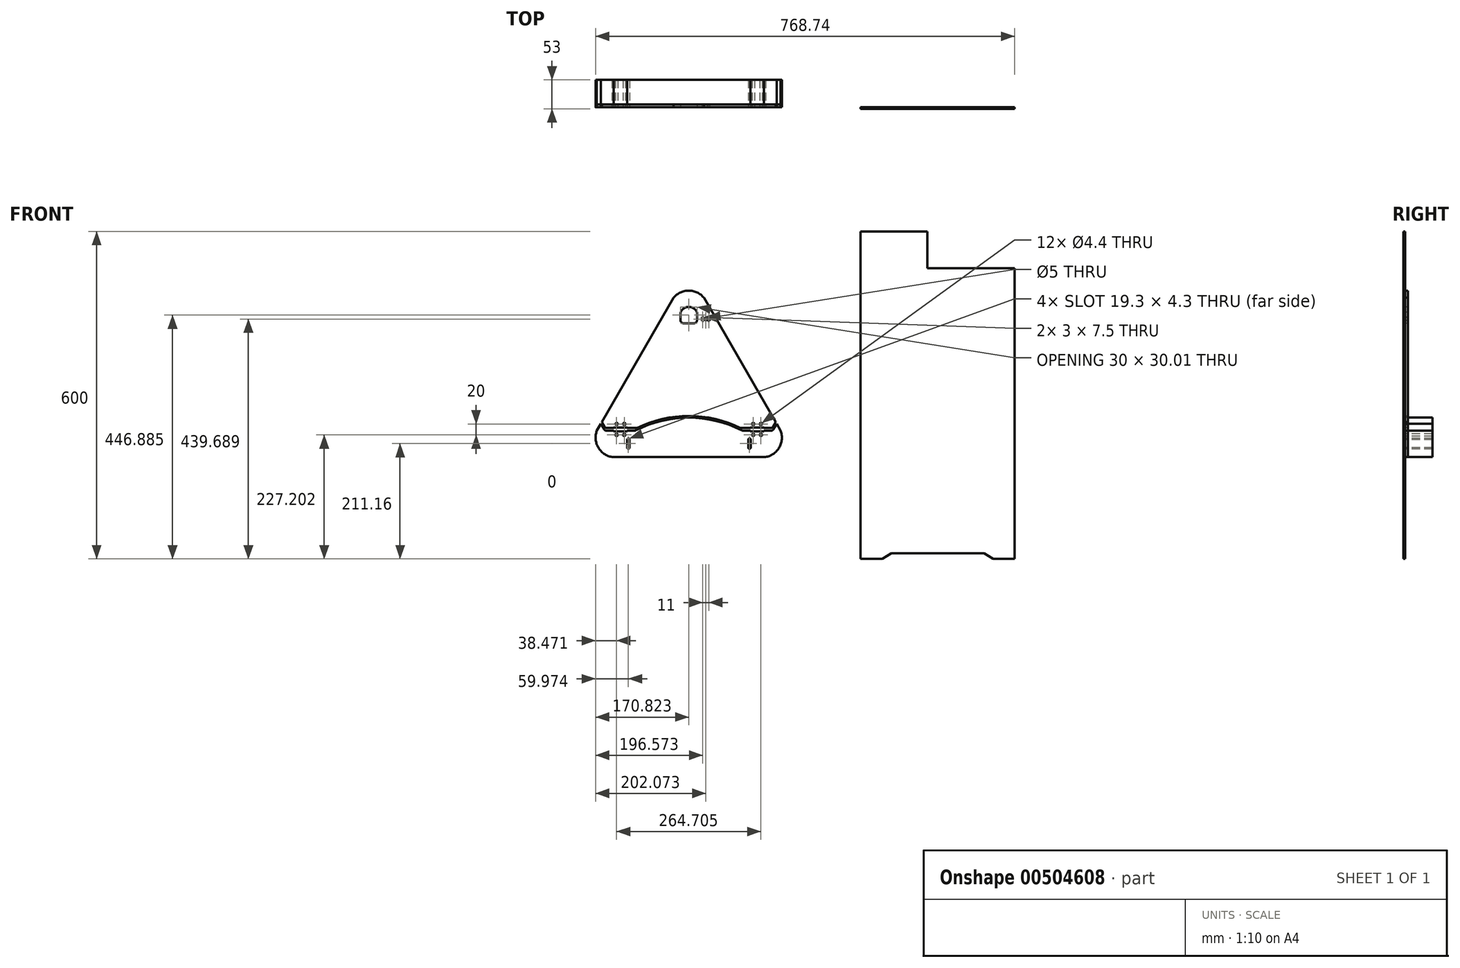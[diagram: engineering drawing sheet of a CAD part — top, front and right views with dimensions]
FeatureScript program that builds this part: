
annotation { "Feature Type Name" : "Feature", "Feature Type Description" : "" }
export const myFeature = defineFeature(function(context is Context, id is Id, definition is map)
    precondition{}
    {
        {
            var Q0;
            Q0=qCreatedBy(makeId("Front.planeOp"),FACE);
            var sketch = newSketch(context, id + "F0", { "sketchPlane" : qUnion([Q0])});
            skLineSegment(sketch, "E0.bottom", {"start": v(-18.5, 300) * mm, "end": v(-141.2, 300) * mm});
            skLineSegment(sketch, "E0.top", {"start": v(141.5, -300) * mm, "end": v(101.5, -300) * mm});
            skLineSegment(sketch, "E0.left", {"start": v(141.5, 233) * mm, "end": v(141.5, -300) * mm});
            skLineSegment(sketch, "E0.right", {"start": v(-141.2, 300) * mm, "end": v(-141.2, -300) * mm});
            skLineSegment(sketch, "E1.top", {"start": v(141.5, 233) * mm, "end": v(-18.5, 233) * mm});
            skLineSegment(sketch, "E1.right", {"start": v(-18.5, 300) * mm, "end": v(-18.5, 233) * mm});
            skLineSegment(sketch, "E2.bottom", {"start": v(186.44, 300) * mm, "end": v(469.14, 300) * mm});
            skLineSegment(sketch, "E2.top", {"start": v(186.44, -300) * mm, "end": v(469.14, -300) * mm});
            skLineSegment(sketch, "E2.left", {"start": v(186.44, 300) * mm, "end": v(186.44, -300) * mm});
            skLineSegment(sketch, "E2.right", {"start": v(469.14, 300) * mm, "end": v(469.14, -300) * mm});
            skLineSegment(sketch, "E3.bottom", {"start": v(-149.47, -443.3) * mm, "end": v(-66.47, -443.3) * mm});
            skLineSegment(sketch, "E3.top", {"start": v(-149.47, -548.3) * mm, "end": v(-71.47, -548.3) * mm});
            skLineSegment(sketch, "E3.left", {"start": v(-149.47, -443.3) * mm, "end": v(-149.47, -548.3) * mm});
            skLineSegment(sketch, "E3.right", {"start": v(-66.47, -443.3) * mm, "end": v(-66.47, -546.3) * mm});
            skLineSegment(sketch, "E4.top", {"start": v(-66.47, -546.3) * mm, "end": v(-71.47, -546.3) * mm});
            skLineSegment(sketch, "E4.right", {"start": v(-71.47, -548.3) * mm, "end": v(-71.47, -546.3) * mm});
            skLineSegment(sketch, "E5.bottom", {"start": v(-34.24, -443.3) * mm, "end": v(248.46, -443.3) * mm});
            skLineSegment(sketch, "E5.top", {"start": v(-34.24, -548.3) * mm, "end": v(248.46, -548.3) * mm});
            skLineSegment(sketch, "E5.left", {"start": v(-34.24, -443.3) * mm, "end": v(-34.24, -548.3) * mm});
            skLineSegment(sketch, "E5.right", {"start": v(248.46, -443.3) * mm, "end": v(248.46, -548.3) * mm});
            skLineSegment(sketch, "E6.bottom", {"start": v(25.76, -515.8) * mm, "end": v(-14.24, -515.8) * mm, "construction": true});
            skLineSegment(sketch, "E6.top", {"start": v(25.76, -475.8) * mm, "end": v(-14.24, -475.8) * mm, "construction": true});
            skLineSegment(sketch, "E6.left", {"start": v(25.76, -515.8) * mm, "end": v(25.76, -475.8) * mm, "construction": true});
            skLineSegment(sketch, "E6.right", {"start": v(-14.24, -515.8) * mm, "end": v(-14.24, -475.8) * mm, "construction": true});
            skPoint(sketch, "E6.middle", {"position": v(5.76, -495.8) * mm});
            skCircle(sketch, "E7", {"center": v(-10.24, -511.8) * mm, "radius": 1.8 * mm});
            skCircle(sketch, "E8.0.1.0", {"center": v(-10.24, -479.8) * mm, "radius": 1.8 * mm});
            skCircle(sketch, "E8.1.0.0", {"center": v(21.76, -511.8) * mm, "radius": 1.8 * mm});
            skCircle(sketch, "E8.1.1.0", {"center": v(21.76, -479.8) * mm, "radius": 1.8 * mm});
            skLineSegment(sketch, "E8.direction1", {"start": v(-10.24, -511.8) * mm, "end": v(21.76, -511.8) * mm, "construction": true});
            skLineSegment(sketch, "E8.direction2", {"start": v(-10.24, -511.8) * mm, "end": v(-10.24, -479.8) * mm, "construction": true});
            skArc(sketch, "E9", {"start": v(-6.6, -509.57) * mm, "mid": v(5.76, -514.3) * mm, "end": v(18.12, -509.57) * mm});
            skLineSegment(sketch, "E10.left", {"start": v(18.12, -482.03) * mm, "end": v(13.51, -486.64) * mm});
            skLineSegment(sketch, "E10.right", {"start": v(19.53, -483.44) * mm, "end": v(14.93, -488.05) * mm});
            skLineSegment(sketch, "E11.left", {"start": v(-8, -483.44) * mm, "end": v(-3.4, -488.05) * mm});
            skLineSegment(sketch, "E11.right", {"start": v(-6.61, -482) * mm, "end": v(-1.99, -486.64) * mm});
            skCircle(sketch, "E12", {"center": v(5.76, -495.8) * mm, "radius": 11 * mm, "construction": true});
            skArc(sketch, "E13.0", {"start": v(-3.4, -488.05) * mm, "mid": v(-6.24, -495.8) * mm, "end": v(-3.4, -503.55) * mm});
            skArc(sketch, "E14.0", {"start": v(-1.98, -489.47) * mm, "mid": v(-4.24, -495.8) * mm, "end": v(-1.98, -502.13) * mm});
            skLineSegment(sketch, "E15.right", {"start": v(141.46, -473.3) * mm, "end": v(141.46, -518.3) * mm, "construction": true});
            skArc(sketch, "E16.0.startCap", {"start": v(134.96, -473.3) * mm, "mid": v(141.46, -466.8) * mm, "end": v(147.96, -473.3) * mm});
            skArc(sketch, "E16.0.endCap", {"start": v(147.96, -518.3) * mm, "mid": v(141.46, -524.8) * mm, "end": v(134.96, -518.3) * mm});
            skLineSegment(sketch, "E16.0.left", {"start": v(147.96, -473.3) * mm, "end": v(147.96, -518.3) * mm});
            skLineSegment(sketch, "E16.0.right", {"start": v(134.96, -473.3) * mm, "end": v(134.96, -518.3) * mm});
            skLineSegment(sketch, "E17.bottom", {"start": v(279.2, -443.3) * mm, "end": v(561.9, -443.3) * mm});
            skLineSegment(sketch, "E17.top", {"start": v(279.2, -548.3) * mm, "end": v(404.2, -548.3) * mm});
            skLineSegment(sketch, "E17.left", {"start": v(279.2, -443.3) * mm, "end": v(279.2, -548.3) * mm});
            skLineSegment(sketch, "E17.right", {"start": v(561.9, -443.3) * mm, "end": v(561.9, -537.3) * mm});
            skLineSegment(sketch, "E18.top", {"start": v(561.9, -537.3) * mm, "end": v(552.9, -537.3) * mm});
            skLineSegment(sketch, "E18.right", {"start": v(404.2, -548.3) * mm, "end": v(404.2, -537.3) * mm});
            skEllipse(sketch, "E19", {"center": v(198.94, 200) * mm, "majorRadius": 3.5 * mm, "minorRadius": 2.5 * mm, "majorAxis": v(1, 0)});
            skEllipse(sketch, "E20.1.0.0", {"center": v(216.44, 200) * mm, "majorRadius": 3.5 * mm, "minorRadius": 2.5 * mm, "majorAxis": v(1, 0)});
            skLineSegment(sketch, "E20.direction1", {"start": v(198.94, 200) * mm, "end": v(216.44, 200) * mm, "construction": true});
            skCircle(sketch, "E21", {"center": v(198.94, 200) * mm, "radius": 2.5 * mm, "construction": true});
            skCircle(sketch, "E22", {"center": v(216.44, 200) * mm, "radius": 2.5 * mm, "construction": true});
            skEllipse(sketch, "E23", {"center": v(439.14, 200) * mm, "majorRadius": 3.5 * mm, "minorRadius": 2.5 * mm, "majorAxis": v(1, 0)});
            skEllipse(sketch, "E24.1.0.0", {"center": v(456.64, 200) * mm, "majorRadius": 3.5 * mm, "minorRadius": 2.5 * mm, "majorAxis": v(1, 0)});
            skLineSegment(sketch, "E24.direction1", {"start": v(439.14, 200) * mm, "end": v(456.64, 200) * mm, "construction": true});
            skCircle(sketch, "E25", {"center": v(439.14, 200) * mm, "radius": 2.5 * mm, "construction": true});
            skCircle(sketch, "E26", {"center": v(456.64, 200) * mm, "radius": 2.5 * mm, "construction": true});
            skEllipse(sketch, "E27", {"center": v(198.94, -200) * mm, "majorRadius": 3.5 * mm, "minorRadius": 2.5 * mm, "majorAxis": v(1, 0)});
            skEllipse(sketch, "E28.1.0.0", {"center": v(216.44, -200) * mm, "majorRadius": 3.5 * mm, "minorRadius": 2.5 * mm, "majorAxis": v(1, 0)});
            skLineSegment(sketch, "E28.direction1", {"start": v(198.94, -200) * mm, "end": v(216.44, -200) * mm, "construction": true});
            skCircle(sketch, "E29", {"center": v(198.94, -200) * mm, "radius": 2.5 * mm, "construction": true});
            skCircle(sketch, "E30", {"center": v(216.44, -200) * mm, "radius": 2.5 * mm, "construction": true});
            skEllipse(sketch, "E31", {"center": v(439.14, -200) * mm, "majorRadius": 3.5 * mm, "minorRadius": 2.5 * mm, "majorAxis": v(1, 0)});
            skEllipse(sketch, "E32.1.0.0", {"center": v(456.64, -200) * mm, "majorRadius": 3.5 * mm, "minorRadius": 2.5 * mm, "majorAxis": v(1, 0)});
            skLineSegment(sketch, "E32.direction1", {"start": v(439.14, -200) * mm, "end": v(456.64, -200) * mm, "construction": true});
            skCircle(sketch, "E33", {"center": v(439.14, -200) * mm, "radius": 2.5 * mm, "construction": true});
            skCircle(sketch, "E34", {"center": v(456.64, -200) * mm, "radius": 2.5 * mm, "construction": true});
            skLineSegment(sketch, "E35.1.0.0", {"start": v(771.14, 300) * mm, "end": v(771.14, -300) * mm});
            skLineSegment(sketch, "E35.1.0.1", {"start": v(488.44, -300) * mm, "end": v(771.14, -300) * mm});
            skLineSegment(sketch, "E35.1.0.2", {"start": v(488.44, 300) * mm, "end": v(771.14, 300) * mm});
            skLineSegment(sketch, "E35.1.0.3", {"start": v(488.44, 300) * mm, "end": v(488.44, -300) * mm});
            skCircle(sketch, "E35.1.0.4", {"center": v(518.44, -200) * mm, "radius": 2.5 * mm, "construction": true});
            skCircle(sketch, "E35.1.0.5", {"center": v(758.64, -200) * mm, "radius": 2.5 * mm, "construction": true});
            skLineSegment(sketch, "E35.1.0.6", {"start": v(500.94, -200) * mm, "end": v(518.44, -200) * mm, "construction": true});
            skEllipse(sketch, "E35.1.0.7", {"center": v(518.44, 200) * mm, "majorRadius": 3.5 * mm, "minorRadius": 2.5 * mm, "majorAxis": v(1, 0)});
            skEllipse(sketch, "E35.1.0.8", {"center": v(500.94, -200) * mm, "majorRadius": 3.5 * mm, "minorRadius": 2.5 * mm, "majorAxis": v(1, 0)});
            skCircle(sketch, "E35.1.0.9", {"center": v(500.94, 200) * mm, "radius": 2.5 * mm, "construction": true});
            skEllipse(sketch, "E35.1.0.10", {"center": v(518.44, -200) * mm, "majorRadius": 3.5 * mm, "minorRadius": 2.5 * mm, "majorAxis": v(1, 0)});
            skCircle(sketch, "E35.1.0.11", {"center": v(758.64, 200) * mm, "radius": 2.5 * mm, "construction": true});
            skCircle(sketch, "E35.1.0.12", {"center": v(500.94, -200) * mm, "radius": 2.5 * mm, "construction": true});
            skCircle(sketch, "E35.1.0.13", {"center": v(518.44, 200) * mm, "radius": 2.5 * mm, "construction": true});
            skEllipse(sketch, "E35.1.0.14", {"center": v(500.94, 200) * mm, "majorRadius": 3.5 * mm, "minorRadius": 2.5 * mm, "majorAxis": v(1, 0)});
            skLineSegment(sketch, "E35.1.0.15", {"start": v(500.94, 200) * mm, "end": v(518.44, 200) * mm, "construction": true});
            skCircle(sketch, "E35.1.0.16", {"center": v(741.14, 200) * mm, "radius": 2.5 * mm, "construction": true});
            skCircle(sketch, "E35.1.0.17", {"center": v(741.14, -200) * mm, "radius": 2.5 * mm, "construction": true});
            skEllipse(sketch, "E35.1.0.18", {"center": v(758.64, 200) * mm, "majorRadius": 3.5 * mm, "minorRadius": 2.5 * mm, "majorAxis": v(1, 0)});
            skLineSegment(sketch, "E35.1.0.19", {"start": v(741.14, -200) * mm, "end": v(758.64, -200) * mm, "construction": true});
            skLineSegment(sketch, "E35.1.0.20", {"start": v(741.14, 200) * mm, "end": v(758.64, 200) * mm, "construction": true});
            skEllipse(sketch, "E35.1.0.21", {"center": v(758.64, -200) * mm, "majorRadius": 3.5 * mm, "minorRadius": 2.5 * mm, "majorAxis": v(1, 0)});
            skEllipse(sketch, "E35.1.0.22", {"center": v(741.14, -200) * mm, "majorRadius": 3.5 * mm, "minorRadius": 2.5 * mm, "majorAxis": v(1, 0)});
            skEllipse(sketch, "E35.1.0.23", {"center": v(741.14, 200) * mm, "majorRadius": 3.5 * mm, "minorRadius": 2.5 * mm, "majorAxis": v(1, 0)});
            skLineSegment(sketch, "E35.direction1", {"start": v(186.44, -300) * mm, "end": v(488.44, -300) * mm, "construction": true});
            skEllipse(sketch, "E36", {"center": v(531.9, -458.3) * mm, "majorRadius": 3.5 * mm, "minorRadius": 2.5 * mm, "majorAxis": v(1, 0)});
            skEllipse(sketch, "E37.1.0.0", {"center": v(549.4, -458.3) * mm, "majorRadius": 3.5 * mm, "minorRadius": 2.5 * mm, "majorAxis": v(1, 0), "construction": true});
            skLineSegment(sketch, "E37.direction1", {"start": v(531.9, -458.3) * mm, "end": v(549.4, -458.3) * mm, "construction": true});
            skCircle(sketch, "E38", {"center": v(531.9, -458.3) * mm, "radius": 2.5 * mm, "construction": true});
            skCircle(sketch, "E39", {"center": v(549.4, -458.3) * mm, "radius": 2.5 * mm, "construction": true});
            skCircle(sketch, "E40", {"center": v(549.4, -458.3) * mm, "radius": 1.75 * mm});
            skCircle(sketch, "E41", {"center": v(458.4, -458.3) * mm, "radius": 1.75 * mm});
            skLineSegment(sketch, "E42", {"start": v(458.4, -458.3) * mm, "end": v(576.67, -458.3) * mm, "construction": true});
            skEllipse(sketch, "E43", {"center": v(291.7, -458.3) * mm, "majorRadius": 3.5 * mm, "minorRadius": 2.5 * mm, "majorAxis": v(1, 0)});
            skEllipse(sketch, "E44.1.0.0", {"center": v(309.2, -458.3) * mm, "majorRadius": 3.5 * mm, "minorRadius": 2.5 * mm, "majorAxis": v(1, 0)});
            skLineSegment(sketch, "E44.direction1", {"start": v(291.7, -458.3) * mm, "end": v(309.2, -458.3) * mm, "construction": true});
            skCircle(sketch, "E45", {"center": v(291.7, -458.3) * mm, "radius": 2.5 * mm, "construction": true});
            skCircle(sketch, "E46", {"center": v(309.2, -458.3) * mm, "radius": 2.5 * mm, "construction": true});
            skEllipse(sketch, "E47", {"center": v(218.46, -458.3) * mm, "majorRadius": 3.5 * mm, "minorRadius": 2.5 * mm, "majorAxis": v(1, 0)});
            skEllipse(sketch, "E48.1.0.0", {"center": v(235.96, -458.3) * mm, "majorRadius": 3.5 * mm, "minorRadius": 2.5 * mm, "majorAxis": v(1, 0)});
            skLineSegment(sketch, "E48.direction1", {"start": v(218.46, -458.3) * mm, "end": v(235.96, -458.3) * mm, "construction": true});
            skCircle(sketch, "E49", {"center": v(218.46, -458.3) * mm, "radius": 2.5 * mm, "construction": true});
            skCircle(sketch, "E50", {"center": v(235.96, -458.3) * mm, "radius": 2.5 * mm, "construction": true});
            skEllipse(sketch, "E51", {"center": v(218.46, -534.3) * mm, "majorRadius": 3.5 * mm, "minorRadius": 2.5 * mm, "majorAxis": v(1, 0)});
            skEllipse(sketch, "E52.1.0.0", {"center": v(235.96, -534.3) * mm, "majorRadius": 3.5 * mm, "minorRadius": 2.5 * mm, "majorAxis": v(1, 0)});
            skLineSegment(sketch, "E52.direction1", {"start": v(218.46, -534.3) * mm, "end": v(235.96, -534.3) * mm, "construction": true});
            skCircle(sketch, "E53", {"center": v(218.46, -534.3) * mm, "radius": 2.5 * mm, "construction": true});
            skCircle(sketch, "E54", {"center": v(235.96, -534.3) * mm, "radius": 2.5 * mm, "construction": true});
            skEllipse(sketch, "E55", {"center": v(291.7, -534.3) * mm, "majorRadius": 3.5 * mm, "minorRadius": 2.5 * mm, "majorAxis": v(1, 0)});
            skEllipse(sketch, "E56.1.0.0", {"center": v(309.2, -534.3) * mm, "majorRadius": 3.5 * mm, "minorRadius": 2.5 * mm, "majorAxis": v(1, 0)});
            skLineSegment(sketch, "E56.direction1", {"start": v(291.7, -534.3) * mm, "end": v(309.2, -534.3) * mm, "construction": true});
            skCircle(sketch, "E57", {"center": v(291.7, -534.3) * mm, "radius": 2.5 * mm, "construction": true});
            skCircle(sketch, "E58", {"center": v(309.2, -534.3) * mm, "radius": 2.5 * mm, "construction": true});
            skEllipticalArc(sketch, "E59", {});
            skEllipticalArc(sketch, "E60.1.0.0", {});
            skLineSegment(sketch, "E60.direction1", {"start": v(531.9, -534.3) * mm, "end": v(549.4, -534.3) * mm, "construction": true});
            skCircle(sketch, "E61", {"center": v(531.9, -534.3) * mm, "radius": 2.5 * mm, "construction": true});
            skCircle(sketch, "E62", {"center": v(549.4, -534.3) * mm, "radius": 2.5 * mm, "construction": true});
            skEllipse(sketch, "E63", {"center": v(-21.74, -458.3) * mm, "majorRadius": 3.5 * mm, "minorRadius": 2.5 * mm, "majorAxis": v(1, 0)});
            skEllipse(sketch, "E64.1.0.0", {"center": v(-4.24, -458.3) * mm, "majorRadius": 3.5 * mm, "minorRadius": 2.5 * mm, "majorAxis": v(1, 0)});
            skLineSegment(sketch, "E64.direction1", {"start": v(-21.74, -458.3) * mm, "end": v(-4.24, -458.3) * mm, "construction": true});
            skCircle(sketch, "E65", {"center": v(-21.74, -458.3) * mm, "radius": 2.5 * mm, "construction": true});
            skCircle(sketch, "E66", {"center": v(-4.24, -458.3) * mm, "radius": 2.5 * mm, "construction": true});
            skEllipse(sketch, "E67", {"center": v(-21.74, -534.3) * mm, "majorRadius": 3.5 * mm, "minorRadius": 2.5 * mm, "majorAxis": v(1, 0)});
            skEllipse(sketch, "E68.1.0.0", {"center": v(-4.24, -534.3) * mm, "majorRadius": 3.5 * mm, "minorRadius": 2.5 * mm, "majorAxis": v(1, 0)});
            skLineSegment(sketch, "E68.direction1", {"start": v(-21.74, -534.3) * mm, "end": v(-4.24, -534.3) * mm, "construction": true});
            skCircle(sketch, "E69", {"center": v(-21.74, -534.3) * mm, "radius": 2.5 * mm, "construction": true});
            skCircle(sketch, "E70", {"center": v(-4.24, -534.3) * mm, "radius": 2.5 * mm, "construction": true});
            skEllipse(sketch, "E71", {"center": v(-136.97, -458.3) * mm, "majorRadius": 3.5 * mm, "minorRadius": 2.5 * mm, "majorAxis": v(1, 0)});
            skEllipse(sketch, "E72.1.0.0", {"center": v(-119.47, -458.3) * mm, "majorRadius": 3.5 * mm, "minorRadius": 2.5 * mm, "majorAxis": v(1, 0)});
            skLineSegment(sketch, "E72.direction1", {"start": v(-136.97, -458.3) * mm, "end": v(-119.47, -458.3) * mm, "construction": true});
            skCircle(sketch, "E73", {"center": v(-136.97, -458.3) * mm, "radius": 2.5 * mm, "construction": true});
            skCircle(sketch, "E74", {"center": v(-119.47, -458.3) * mm, "radius": 2.5 * mm, "construction": true});
            skEllipse(sketch, "E75", {"center": v(-136.97, -534.3) * mm, "majorRadius": 3.5 * mm, "minorRadius": 2.5 * mm, "majorAxis": v(1, 0)});
            skEllipse(sketch, "E76.1.0.0", {"center": v(-119.47, -534.3) * mm, "majorRadius": 3.5 * mm, "minorRadius": 2.5 * mm, "majorAxis": v(1, 0)});
            skLineSegment(sketch, "E76.direction1", {"start": v(-136.97, -534.3) * mm, "end": v(-119.47, -534.3) * mm, "construction": true});
            skCircle(sketch, "E77", {"center": v(-136.97, -534.3) * mm, "radius": 2.5 * mm, "construction": true});
            skCircle(sketch, "E78", {"center": v(-119.47, -534.3) * mm, "radius": 2.5 * mm, "construction": true});
            skLineSegment(sketch, "E79", {"start": v(528.4, -534.3) * mm, "end": v(528.4, -537.3) * mm});
            skLineSegment(sketch, "E80", {"start": v(535.4, -534.3) * mm, "end": v(535.4, -537.3) * mm});
            skLineSegment(sketch, "E81", {"start": v(545.9, -534.3) * mm, "end": v(545.9, -537.3) * mm});
            skLineSegment(sketch, "E82", {"start": v(552.9, -534.3) * mm, "end": v(552.9, -537.3) * mm});
            skLineSegment(sketch, "E83.trimOffspring", {"start": v(528.4, -537.3) * mm, "end": v(404.2, -537.3) * mm});
            skLineSegment(sketch, "E84.trimOffspring", {"start": v(545.9, -537.3) * mm, "end": v(535.4, -537.3) * mm});
            skLineSegment(sketch, "E85", {"start": v(-85, -290) * mm, "end": v(85, -290) * mm});
            skPoint(sketch, "E86", {"position": v(0, -290) * mm});
            skPoint(sketch, "E87", {"position": v(-101.2, -300) * mm});
            skLineSegment(sketch, "E88", {"start": v(-101.2, -300) * mm, "end": v(-85, -290) * mm});
            skLineSegment(sketch, "E89.trimOffspring", {"start": v(-101.2, -300) * mm, "end": v(-141.2, -300) * mm});
            skPoint(sketch, "E90", {"position": v(101.5, -300) * mm});
            skLineSegment(sketch, "E91", {"start": v(85, -290) * mm, "end": v(101.5, -300) * mm});
            skLineSegment(sketch, "E92.trimOffspring", {"start": v(7.18, -495.8) * mm, "end": v(13.5, -502.13) * mm});
            skLineSegment(sketch, "E93.trimOffspring", {"start": v(5.76, -497.21) * mm, "end": v(12.1, -503.54) * mm});
            skLineSegment(sketch, "E94.trimOffspring", {"start": v(4.35, -495.8) * mm, "end": v(-1.98, -502.13) * mm});
            skLineSegment(sketch, "E95.trimOffspring", {"start": v(5.76, -497.21) * mm, "end": v(-0.57, -503.54) * mm});
            skArc(sketch, "E96.trimOffspring", {"start": v(19.53, -508.15) * mm, "mid": v(24.26, -495.8) * mm, "end": v(19.53, -483.44) * mm});
            skArc(sketch, "E97.trimOffspring", {"start": v(18.12, -482.03) * mm, "mid": v(5.76, -477.3) * mm, "end": v(-6.6, -482.03) * mm});
            skArc(sketch, "E98.trimOffspring", {"start": v(-8, -483.44) * mm, "mid": v(-12.74, -495.8) * mm, "end": v(-8, -508.15) * mm});
            skCircle(sketch, "E99.0.1.0", {"center": v(458.4, -534.3) * mm, "radius": 1.75 * mm});
            skLineSegment(sketch, "E99.direction1", {"start": v(458.4, -458.3) * mm, "end": v(483.4, -458.3) * mm, "construction": true});
            skLineSegment(sketch, "E99.direction2", {"start": v(458.4, -458.3) * mm, "end": v(458.4, -534.3) * mm, "construction": true});
            skLineSegment(sketch, "E100.trimOffspring", {"start": v(-3.4, -503.55) * mm, "end": v(-8, -508.15) * mm});
            skLineSegment(sketch, "E101.trimOffspring", {"start": v(-1.99, -504.96) * mm, "end": v(-6.6, -509.57) * mm});
            skLineSegment(sketch, "E102.trimOffspring", {"start": v(14.93, -503.55) * mm, "end": v(19.55, -508.17) * mm});
            skLineSegment(sketch, "E103.trimOffspring", {"start": v(13.51, -504.96) * mm, "end": v(18.14, -509.59) * mm});
            skLineSegment(sketch, "E104.trimOffspring", {"start": v(-0.57, -488.06) * mm, "end": v(5.76, -494.38) * mm});
            skLineSegment(sketch, "E105.trimOffspring", {"start": v(-1.98, -489.47) * mm, "end": v(4.35, -495.8) * mm});
            skLineSegment(sketch, "E106.trimOffspring", {"start": v(12.1, -488.06) * mm, "end": v(5.76, -494.38) * mm});
            skLineSegment(sketch, "E107.trimOffspring", {"start": v(13.5, -489.47) * mm, "end": v(7.18, -495.8) * mm});
            skArc(sketch, "E108.trimOffspring", {"start": v(12.1, -488.06) * mm, "mid": v(5.76, -485.8) * mm, "end": v(-0.57, -488.06) * mm});
            skArc(sketch, "E109.trimOffspring", {"start": v(13.51, -486.64) * mm, "mid": v(5.76, -483.8) * mm, "end": v(-1.99, -486.64) * mm});
            skArc(sketch, "E110.trimOffspring", {"start": v(13.5, -502.13) * mm, "mid": v(15.76, -495.8) * mm, "end": v(13.5, -489.47) * mm});
            skArc(sketch, "E111.trimOffspring", {"start": v(14.93, -503.55) * mm, "mid": v(17.76, -495.8) * mm, "end": v(14.93, -488.05) * mm});
            skArc(sketch, "E112.trimOffspring", {"start": v(-1.99, -504.96) * mm, "mid": v(5.76, -507.8) * mm, "end": v(13.51, -504.96) * mm});
            skArc(sketch, "E113.trimOffspring", {"start": v(-0.57, -503.54) * mm, "mid": v(5.76, -505.8) * mm, "end": v(12.1, -503.54) * mm});
            const initialGuessF0  = {"E59": [0.5318984677314759, -0.5342984781265259, 1, 0, 0.0035, 0.0025, 0, 3.141592653589793], "E60.1.0.0": [0.5493984677314758, -0.5342984781265259, 1, 0, 0.0035, 0.0025, 0, 3.141592653589793]};
            skSetInitialGuess(sketch, initialGuessF0);
            skSolve(sketch);
        }
        {
            var Q0;
            Q0=makeQuery(id+"F0.imprint","IMPRINT",FACE,{"disambiguationData":[TD([[makeQuery(id+"F0.imprint","IMPRINT",EDGE,{"derivedFrom":sQuery(id+"F0.wireOp",EDGE,"E0.bottom")}),1.0]])]});
            extrude(context, id + "F1", {"entities" : qUnion([Q0]), "depth" : 3 * mm});
        }
        {
            var Q0;
            Q0=qCreatedBy(makeId("Front.planeOp"),FACE);
            var sketch = newSketch(context, id + "F2", { "sketchPlane" : qUnion([Q0])});
            skLineSegment(sketch, "E114", {"start": v(-567.99, 54.45) * mm, "end": v(-344.84, 54.45) * mm, "construction": true});
            skLineSegment(sketch, "E115", {"start": v(-456.42, 178.66) * mm, "end": v(-456.42, 161.88) * mm, "construction": true});
            skArc(sketch, "E116", {"start": v(-428.67, 178.66) * mm, "mid": v(-456.42, 191.66) * mm, "end": v(-484.17, 178.66) * mm});
            skLineSegment(sketch, "E117", {"start": v(-597.77, -113.34) * mm, "end": v(-315.07, -113.34) * mm, "construction": true});
            skArc(sketch, "E118.1.0", {"start": v(-625.02, -65.3) * mm, "mid": v(-622.4, -95.83) * mm, "end": v(-597.27, -113.36) * mm});
            skArc(sketch, "E118.2.0", {"start": v(-315.57, -113.36) * mm, "mid": v(-290.43, -95.83) * mm, "end": v(-287.82, -65.3) * mm});
            skPoint(sketch, "E118.center", {"position": v(-456.42, 0) * mm});
            skLineSegment(sketch, "E119", {"start": v(-290.75, -60.21) * mm, "end": v(-295.28, -52.38) * mm});
            skLineSegment(sketch, "E120", {"start": v(-315.57, -113.36) * mm, "end": v(-597.27, -113.36) * mm});
            skLineSegment(sketch, "E121", {"start": v(-622.18, -60.38) * mm, "end": v(-617.56, -52.38) * mm});
            skLineSegment(sketch, "E122", {"start": v(-607.2, -65.3) * mm, "end": v(-594.22, -65.3) * mm});
            skLineSegment(sketch, "E123.bottom", {"start": v(-456, 161.88) * mm, "end": v(-456.84, 161.88) * mm});
            skLineSegment(sketch, "E123.top", {"start": v(-446.42, 131.88) * mm, "end": v(-466.42, 131.88) * mm});
            skLineSegment(sketch, "E123.left", {"start": v(-441.42, 151.88) * mm, "end": v(-441.42, 136.88) * mm});
            skLineSegment(sketch, "E123.right", {"start": v(-471.42, 151.88) * mm, "end": v(-471.42, 136.88) * mm});
            skPoint(sketch, "E123.middle", {"position": v(-456.42, 146.88) * mm});
            skArc(sketch, "E124", {"start": v(-441.42, 151.88) * mm, "mid": v(-456.42, 161.89) * mm, "end": v(-471.42, 151.88) * mm});
            skPoint(sketch, "E125.orphan", {"position": v(-471.42, 161.88) * mm});
            skPoint(sketch, "E126.orphan", {"position": v(-441.42, 161.88) * mm});
            skLineSegment(sketch, "E127.trimOffspring", {"start": v(-456.42, 54.45) * mm, "end": v(-456.42, -113.34) * mm, "construction": true});
            skArc(sketch, "E128", {"start": v(-358.88, -64.75) * mm, "mid": v(-456.42, -41.2) * mm, "end": v(-553.95, -64.75) * mm});
            skArc(sketch, "E129.0", {"start": v(-362.08, -59.8) * mm, "mid": v(-456.42, -38.2) * mm, "end": v(-550.75, -59.8) * mm});
            skLineSegment(sketch, "E130.trimOffspring", {"start": v(-359.9, -60.3) * mm, "end": v(-343.61, -60.3) * mm});
            skLineSegment(sketch, "E131", {"start": v(-625.02, -65.3) * mm, "end": v(-597.27, -113.36) * mm, "construction": true});
            skLineSegment(sketch, "E132", {"start": v(-315.02, -113.26) * mm, "end": v(-315.07, -113.34) * mm});
            skLineSegment(sketch, "E133", {"start": v(-617.56, -52.38) * mm, "end": v(-613.06, -60.17) * mm});
            skLineSegment(sketch, "E134.0", {"start": v(-615.82, -49.38) * mm, "end": v(-610.96, -57.8) * mm});
            skLineSegment(sketch, "E135", {"start": v(-625.02, -65.3) * mm, "end": v(-622.18, -60.38) * mm});
            skLineSegment(sketch, "E136", {"start": v(-578.9, -113.34) * mm, "end": v(-578.88, -113.36) * mm});
            skLineSegment(sketch, "E137", {"start": v(-610.1, -65.3) * mm, "end": v(-582.34, -113.36) * mm, "construction": true});
            skLineSegment(sketch, "E138", {"start": v(-613.06, -60.17) * mm, "end": v(-611.54, -62.8) * mm});
            skLineSegment(sketch, "E139.trimOffspring", {"start": v(-615.82, -49.38) * mm, "end": v(-484.17, 178.66) * mm});
            skLineSegment(sketch, "E140.trimOffspring", {"start": v(-606.63, -60.3) * mm, "end": v(-594.22, -60.3) * mm});
            skLineSegment(sketch, "E141.trimOffspring", {"start": v(-356.6, -65.3) * mm, "end": v(-343.61, -65.3) * mm});
            skLineSegment(sketch, "E142.MirrorCS", {"start": v(-602.63, -52.38) * mm, "end": v(-574.88, -100.44) * mm, "construction": true});
            skLineSegment(sketch, "E143.MirrorCS", {"start": v(-302.74, -65.3) * mm, "end": v(-330.49, -113.36) * mm, "construction": true});
            skLineSegment(sketch, "E144.MirrorCS", {"start": v(-297.01, -49.38) * mm, "end": v(-301.87, -57.8) * mm});
            skLineSegment(sketch, "E145", {"start": v(-301.3, -62.8) * mm, "end": v(-295.28, -52.38) * mm});
            skLineSegment(sketch, "E146", {"start": v(-290.75, -60.21) * mm, "end": v(-287.82, -65.3) * mm});
            skLineSegment(sketch, "E147.trimOffspring", {"start": v(-297.01, -49.38) * mm, "end": v(-428.67, 178.66) * mm});
            skPoint(sketch, "E148.visualSharp", {"position": v(-610.1, -65.3) * mm});
            skArc(sketch, "E148.filletArc", {"start": v(-611.54, -62.8) * mm, "mid": v(-609.7, -64.63) * mm, "end": v(-607.2, -65.3) * mm});
            skPoint(sketch, "E149.visualSharp", {"position": v(-609.52, -60.3) * mm});
            skArc(sketch, "E149.filletArc", {"start": v(-610.96, -57.8) * mm, "mid": v(-609.13, -59.63) * mm, "end": v(-606.63, -60.3) * mm});
            skPoint(sketch, "E150.visualSharp", {"position": v(-551.77, -60.3) * mm});
            skArc(sketch, "E150.filletArc", {"start": v(-552.93, -60.3) * mm, "mid": v(-551.8, -60.17) * mm, "end": v(-550.75, -59.8) * mm});
            skPoint(sketch, "E151.visualSharp", {"position": v(-555.02, -65.3) * mm});
            skArc(sketch, "E151.filletArc", {"start": v(-556.23, -65.3) * mm, "mid": v(-555.06, -65.16) * mm, "end": v(-553.95, -64.75) * mm});
            skPoint(sketch, "E152.visualSharp", {"position": v(-361.06, -60.3) * mm});
            skArc(sketch, "E152.filletArc", {"start": v(-362.08, -59.8) * mm, "mid": v(-361.02, -60.17) * mm, "end": v(-359.9, -60.3) * mm});
            skPoint(sketch, "E153.visualSharp", {"position": v(-357.82, -65.3) * mm});
            skArc(sketch, "E153.filletArc", {"start": v(-358.88, -64.75) * mm, "mid": v(-357.78, -65.16) * mm, "end": v(-356.6, -65.3) * mm});
            skPoint(sketch, "E154.visualSharp", {"position": v(-303.32, -60.3) * mm});
            skArc(sketch, "E154.filletArc", {"start": v(-306.2, -60.3) * mm, "mid": v(-303.7, -59.63) * mm, "end": v(-301.87, -57.8) * mm});
            skPoint(sketch, "E155.visualSharp", {"position": v(-302.74, -65.3) * mm});
            skArc(sketch, "E155.filletArc", {"start": v(-305.63, -65.3) * mm, "mid": v(-303.13, -64.63) * mm, "end": v(-301.3, -62.8) * mm});
            skPoint(sketch, "E156.visualSharp", {"position": v(-471.42, 131.88) * mm});
            skArc(sketch, "E156.filletArc", {"start": v(-471.42, 136.88) * mm, "mid": v(-469.95, 133.35) * mm, "end": v(-466.42, 131.88) * mm});
            skPoint(sketch, "E157.visualSharp", {"position": v(-441.42, 131.88) * mm});
            skArc(sketch, "E157.filletArc", {"start": v(-446.42, 131.88) * mm, "mid": v(-442.88, 133.35) * mm, "end": v(-441.42, 136.88) * mm});
            skPoint(sketch, "E158", {"position": v(-581.72, -65.3) * mm});
            skCircle(sketch, "E159", {"center": v(-588.77, -72.8) * mm, "radius": 2.2 * mm});
            skCircle(sketch, "E160", {"center": v(-574.67, -72.8) * mm, "radius": 2.2 * mm});
            skLineSegment(sketch, "E161", {"start": v(-588.77, -72.8) * mm, "end": v(-574.67, -72.8) * mm, "construction": true});
            skPoint(sketch, "E162", {"position": v(-581.72, -72.8) * mm});
            skCircle(sketch, "E163.0.1.0", {"center": v(-588.77, -52.8) * mm, "radius": 2.2 * mm});
            skCircle(sketch, "E163.0.1.1", {"center": v(-574.67, -52.8) * mm, "radius": 2.2 * mm});
            skLineSegment(sketch, "E163.direction1", {"start": v(-588.77, -72.8) * mm, "end": v(-562.72, -72.8) * mm, "construction": true});
            skLineSegment(sketch, "E163.direction2", {"start": v(-588.77, -72.8) * mm, "end": v(-588.77, -52.8) * mm, "construction": true});
            skPoint(sketch, "E164", {"position": v(-569.22, -65.3) * mm});
            skPoint(sketch, "E165", {"position": v(-594.22, -65.3) * mm});
            skPoint(sketch, "E166", {"position": v(-594.22, -60.3) * mm});
            skPoint(sketch, "E167", {"position": v(-569.22, -60.3) * mm});
            skLineSegment(sketch, "E168", {"start": v(-594.22, -60.3) * mm, "end": v(-594.22, -59.3) * mm});
            skLineSegment(sketch, "E169", {"start": v(-594.22, -59.3) * mm, "end": v(-569.22, -59.3) * mm});
            skLineSegment(sketch, "E170", {"start": v(-569.22, -59.3) * mm, "end": v(-569.22, -60.3) * mm});
            skLineSegment(sketch, "E171", {"start": v(-594.22, -65.3) * mm, "end": v(-594.22, -66.36) * mm});
            skLineSegment(sketch, "E172", {"start": v(-594.22, -66.36) * mm, "end": v(-569.22, -66.36) * mm});
            skLineSegment(sketch, "E173", {"start": v(-569.22, -66.36) * mm, "end": v(-569.22, -65.3) * mm});
            skLineSegment(sketch, "E174.trimOffspring", {"start": v(-569.22, -60.3) * mm, "end": v(-552.93, -60.3) * mm});
            skLineSegment(sketch, "E175.trimOffspring", {"start": v(-569.22, -65.3) * mm, "end": v(-556.23, -65.3) * mm});
            skPoint(sketch, "E176", {"position": v(-331.11, -65.3) * mm});
            skCircle(sketch, "E177.1.0.0", {"center": v(-338.16, -52.8) * mm, "radius": 2.2 * mm});
            skCircle(sketch, "E177.1.0.1", {"center": v(-324.06, -52.8) * mm, "radius": 2.2 * mm});
            skLineSegment(sketch, "E177.1.0.2", {"start": v(-343.61, -59.3) * mm, "end": v(-318.61, -59.3) * mm});
            skLineSegment(sketch, "E177.1.0.3", {"start": v(-343.61, -66.36) * mm, "end": v(-318.61, -66.36) * mm});
            skCircle(sketch, "E177.1.0.4", {"center": v(-338.16, -72.8) * mm, "radius": 2.2 * mm});
            skCircle(sketch, "E177.1.0.5", {"center": v(-324.06, -72.8) * mm, "radius": 2.2 * mm});
            skLineSegment(sketch, "E177.direction1", {"start": v(-588.77, -52.8) * mm, "end": v(-338.16, -52.8) * mm, "construction": true});
            skLineSegment(sketch, "E178", {"start": v(-343.61, -59.3) * mm, "end": v(-343.61, -60.3) * mm});
            skLineSegment(sketch, "E179", {"start": v(-318.61, -59.3) * mm, "end": v(-318.61, -60.3) * mm});
            skLineSegment(sketch, "E180", {"start": v(-318.61, -66.36) * mm, "end": v(-318.61, -65.3) * mm});
            skLineSegment(sketch, "E181", {"start": v(-343.61, -66.36) * mm, "end": v(-343.61, -65.3) * mm});
            skLineSegment(sketch, "E182.trimOffspring", {"start": v(-318.61, -60.3) * mm, "end": v(-306.2, -60.3) * mm});
            skLineSegment(sketch, "E183.trimOffspring", {"start": v(-318.61, -65.3) * mm, "end": v(-305.63, -65.3) * mm});
            skPoint(sketch, "E184", {"position": v(-406.17, 139.69) * mm});
            skLineSegment(sketch, "E185", {"start": v(-406.17, 139.69) * mm, "end": v(-436.17, 139.69) * mm, "construction": true});
            skCircle(sketch, "E186", {"center": v(-425.17, 139.69) * mm, "radius": 9 * mm, "construction": true});
            skLineSegment(sketch, "E187.1.0.0", {"start": v(-1111.86, -49.47) * mm, "end": v(-980.17, 178.7) * mm, "construction": true});
            skLineSegment(sketch, "E187.1.0.1", {"start": v(-793.08, -48.28) * mm, "end": v(-821.97, 1.76) * mm, "construction": true});
            skArc(sketch, "E187.1.0.3", {"start": v(-1121.58, -66.31) * mm, "mid": v(-1118.82, -96.44) * mm, "end": v(-1094.12, -113.9) * mm, "construction": true});
            skArc(sketch, "E187.1.0.4", {"start": v(-810.68, -113.9) * mm, "mid": v(-785.47, -96.35) * mm, "end": v(-782.88, -65.74) * mm, "construction": true});
            skArc(sketch, "E187.1.0.5", {"start": v(-924.41, 179.2) * mm, "mid": v(-951.97, 192.15) * mm, "end": v(-979.64, 179.43) * mm, "construction": true});
            skLineSegment(sketch, "E188", {"start": v(-1121.58, -66.31) * mm, "end": v(-1111.86, -49.47) * mm, "construction": true});
            skLineSegment(sketch, "E189", {"start": v(-782.88, -65.74) * mm, "end": v(-793.08, -48.28) * mm, "construction": true});
            skLineSegment(sketch, "E190", {"start": v(-1094.12, -113.9) * mm, "end": v(-810.68, -113.9) * mm, "construction": true});
            skLineSegment(sketch, "E191", {"start": v(-979.95, 179.07) * mm, "end": v(-924.41, 179.2) * mm, "construction": true});
            skLineSegment(sketch, "E192", {"start": v(-1094.12, -113.9) * mm, "end": v(-1121.58, -66.31) * mm, "construction": true});
            skLineSegment(sketch, "E193", {"start": v(-810.68, -113.9) * mm, "end": v(-782.88, -65.74) * mm, "construction": true});
            skLineSegment(sketch, "E194.0", {"start": v(-1114.66, -66.31) * mm, "end": v(-1106.67, -52.47) * mm});
            skLineSegment(sketch, "E194.1", {"start": v(-1090.65, -107.9) * mm, "end": v(-1095.31, -99.82) * mm});
            skLineSegment(sketch, "E194.2", {"start": v(-1106.67, -52.47) * mm, "end": v(-1078.4, -3.49) * mm});
            skLineSegment(sketch, "E194.3", {"start": v(-1090.65, -107.9) * mm, "end": v(-1023.68, -107.9) * mm});
            skLineSegment(sketch, "E194.4", {"start": v(-976.48, 173.08) * mm, "end": v(-967.48, 173.1) * mm});
            skLineSegment(sketch, "E194.5", {"start": v(-798.27, -51.3) * mm, "end": v(-809.57, -31.72) * mm});
            skLineSegment(sketch, "E194.6", {"start": v(-789.82, -65.75) * mm, "end": v(-798.27, -51.3) * mm});
            skLineSegment(sketch, "E194.7", {"start": v(-814.15, -107.9) * mm, "end": v(-809.52, -99.88) * mm});
            skPoint(sketch, "E195.visualSharp", {"position": v(-979.95, 179.07) * mm});
            skArc(sketch, "E195.filletArc", {"start": v(-979.64, 179.43) * mm, "mid": v(-979.92, 179.07) * mm, "end": v(-980.17, 178.7) * mm});
            skLineSegment(sketch, "E196.bottom", {"start": v(-940.48, 149.66) * mm, "end": v(-964.48, 149.66) * mm, "construction": true});
            skLineSegment(sketch, "E196.left", {"start": v(-940.48, 149.66) * mm, "end": v(-940.48, 173.66) * mm, "construction": true});
            skLineSegment(sketch, "E196.right", {"start": v(-964.48, 149.66) * mm, "end": v(-964.48, 173.66) * mm, "construction": true});
            skPoint(sketch, "E196.middle", {"position": v(-952.48, 161.66) * mm});
            skPoint(sketch, "E197", {"position": v(-952.48, 173.66) * mm});
            skLineSegment(sketch, "E198.top", {"start": v(-1076.03, -85.22) * mm, "end": v(-1088.03, -64.44) * mm, "construction": true});
            skLineSegment(sketch, "E198.left", {"start": v(-1096.81, -97.22) * mm, "end": v(-1076.03, -85.22) * mm, "construction": true});
            skLineSegment(sketch, "E198.right", {"start": v(-1108.81, -76.44) * mm, "end": v(-1088.03, -64.44) * mm, "construction": true});
            skPoint(sketch, "E198.middle", {"position": v(-1092.42, -80.83) * mm});
            skPoint(sketch, "E199", {"position": v(-1102.81, -86.83) * mm});
            skPoint(sketch, "E200", {"position": v(-1102.65, -87.1) * mm});
            skLineSegment(sketch, "E201.bottom", {"start": v(-807.99, -97.22) * mm, "end": v(-828.77, -85.22) * mm, "construction": true});
            skLineSegment(sketch, "E201.top", {"start": v(-795.99, -76.43) * mm, "end": v(-816.77, -64.43) * mm, "construction": true});
            skLineSegment(sketch, "E201.right", {"start": v(-828.77, -85.22) * mm, "end": v(-816.77, -64.43) * mm, "construction": true});
            skPoint(sketch, "E201.middle", {"position": v(-812.38, -80.82) * mm});
            skPoint(sketch, "E202", {"position": v(-801.99, -86.82) * mm});
            skLineSegment(sketch, "E203.top", {"start": v(-1069.33, -84.82) * mm, "end": v(-1084.33, -58.84) * mm});
            skLineSegment(sketch, "E203.left", {"start": v(-1095.31, -99.82) * mm, "end": v(-1069.33, -84.82) * mm});
            skLineSegment(sketch, "E203.right", {"start": v(-1110.31, -73.84) * mm, "end": v(-1084.33, -58.84) * mm});
            skPoint(sketch, "E203.middle", {"position": v(-1089.82, -79.33) * mm});
            skLineSegment(sketch, "E204.bottom", {"start": v(-809.52, -99.88) * mm, "end": v(-836.31, -80.62) * mm});
            skLineSegment(sketch, "E204.top", {"start": v(-794.45, -73.77) * mm, "end": v(-821.24, -54.51) * mm});
            skLineSegment(sketch, "E204.right", {"start": v(-836.31, -80.62) * mm, "end": v(-821.24, -54.51) * mm});
            skPoint(sketch, "E204.middle", {"position": v(-815.38, -77.2) * mm});
            skLineSegment(sketch, "E205.bottom", {"start": v(-939.71, 143.66) * mm, "end": v(-967.48, 143.66) * mm});
            skLineSegment(sketch, "E205.right", {"start": v(-967.48, 143.66) * mm, "end": v(-967.48, 173.66) * mm});
            skPoint(sketch, "E205.middle", {"position": v(-952.48, 158.66) * mm});
            skLineSegment(sketch, "E206.trimOffspring", {"start": v(-794.45, -73.77) * mm, "end": v(-789.82, -65.75) * mm});
            skLineSegment(sketch, "E207.trimOffspring", {"start": v(-1110.31, -73.84) * mm, "end": v(-1114.66, -66.31) * mm});
            skPoint(sketch, "E208", {"position": v(-821.97, 1.76) * mm});
            skLineSegment(sketch, "E209.bottom", {"start": v(-939.71, 143.66) * mm, "end": v(-848.8, -13.81) * mm});
            skLineSegment(sketch, "E209.right", {"start": v(-848.8, -13.81) * mm, "end": v(-826.08, -0.62) * mm});
            skPoint(sketch, "E209.middle", {"position": v(-887.93, 84.98) * mm});
            skPoint(sketch, "E210.orphan", {"position": v(-953.88, 168.2) * mm});
            skPoint(sketch, "E205.left.end.orphan", {"position": v(-937.48, 173.66) * mm});
            skPoint(sketch, "E211.orphan", {"position": v(-928.48, 174.24) * mm});
            skPoint(sketch, "E209.left.end.orphan", {"position": v(-927.06, 183.78) * mm});
            skPoint(sketch, "E212.orphan", {"position": v(-937.48, 143.66) * mm});
            skLineSegment(sketch, "E213.bottom", {"start": v(-432.17, 143.44) * mm, "end": v(-429.17, 143.44) * mm});
            skLineSegment(sketch, "E213.top", {"start": v(-432.17, 135.94) * mm, "end": v(-429.17, 135.94) * mm});
            skLineSegment(sketch, "E213.left", {"start": v(-432.17, 143.44) * mm, "end": v(-432.17, 135.94) * mm});
            skLineSegment(sketch, "E213.right", {"start": v(-429.17, 143.44) * mm, "end": v(-429.17, 135.94) * mm});
            skCircle(sketch, "E214", {"center": v(-425.17, 139.69) * mm, "radius": 2.5 * mm});
            skLineSegment(sketch, "E215.bottom", {"start": v(-415.17, 144.69) * mm, "end": v(-435.17, 144.69) * mm, "construction": true});
            skLineSegment(sketch, "E215.top", {"start": v(-415.17, 134.69) * mm, "end": v(-435.17, 134.69) * mm, "construction": true});
            skLineSegment(sketch, "E215.left", {"start": v(-415.17, 144.69) * mm, "end": v(-415.17, 134.69) * mm, "construction": true});
            skLineSegment(sketch, "E215.right", {"start": v(-435.17, 144.69) * mm, "end": v(-435.17, 134.69) * mm, "construction": true});
            skPoint(sketch, "E216", {"position": v(-429.17, 139.69) * mm});
            skLineSegment(sketch, "E217.bottom", {"start": v(-421.17, 143.44) * mm, "end": v(-418.17, 143.44) * mm});
            skLineSegment(sketch, "E217.top", {"start": v(-421.17, 135.94) * mm, "end": v(-418.17, 135.94) * mm});
            skLineSegment(sketch, "E217.left", {"start": v(-421.17, 143.44) * mm, "end": v(-421.17, 135.94) * mm});
            skLineSegment(sketch, "E217.right", {"start": v(-418.17, 143.44) * mm, "end": v(-418.17, 135.94) * mm});
            skLineSegment(sketch, "E218", {"start": v(-967.48, 173.1) * mm, "end": v(-932.32, 173.17) * mm, "construction": true});
            skLineSegment(sketch, "E219", {"start": v(-952.4, -107.9) * mm, "end": v(-951.52, 173.13) * mm, "construction": true});
            skLineSegment(sketch, "E220", {"start": v(-315.02, -113.26) * mm, "end": v(-287.82, -65.3) * mm, "construction": true});
            skPoint(sketch, "E221", {"position": v(-951.96, 32.62) * mm});
            skLineSegment(sketch, "E222", {"start": v(-801.99, -86.82) * mm, "end": v(-1041.57, 60.3) * mm, "construction": true});
            skLineSegment(sketch, "E223", {"start": v(-789.82, -65.75) * mm, "end": v(-806.26, -37.3) * mm, "construction": true});
            skLineSegment(sketch, "E224", {"start": v(-1102.65, -87.1) * mm, "end": v(-859.15, 53.58) * mm, "construction": true});
            skPoint(sketch, "E224.endSnap0", {"position": v(-859.15, 54.24) * mm});
            skCircle(sketch, "E225", {"center": v(-952.05, 2.71) * mm, "radius": 80 * mm, "construction": true});
            skLineSegment(sketch, "E226.0", {"start": v(-1076.22, -119.96) * mm, "end": v(-996.2, 171.58) * mm, "construction": true});
            skLineSegment(sketch, "E226.1", {"start": v(-996.2, 171.58) * mm, "end": v(-783.73, -43.48) * mm, "construction": true});
            skLineSegment(sketch, "E226.2", {"start": v(-783.73, -43.48) * mm, "end": v(-1076.22, -119.96) * mm, "construction": true});
            skPoint(sketch, "E226.0.midPoint", {"position": v(-1039.22, 7) * mm});
            skLineSegment(sketch, "E227", {"start": v(-1076.22, -119.96) * mm, "end": v(-889.97, 64.05) * mm, "construction": true});
            skLineSegment(sketch, "E228", {"start": v(-889.97, 64.05) * mm, "end": v(-1036.26, -80.48) * mm, "construction": true});
            skLineSegment(sketch, "E229", {"start": v(-996.2, 171.58) * mm, "end": v(-929.98, -81.72) * mm, "construction": true});
            skLineSegment(sketch, "E230", {"start": v(-783.73, -43.48) * mm, "end": v(-1036.21, 25.81) * mm, "construction": true});
            skLineSegment(sketch, "E231.bottom", {"start": v(-1003.7, -58.85) * mm, "end": v(-1014.24, -48.18) * mm});
            skLineSegment(sketch, "E231.top", {"start": v(-1017.92, -72.9) * mm, "end": v(-1028.46, -62.23) * mm});
            skLineSegment(sketch, "E231.left", {"start": v(-1003.7, -58.85) * mm, "end": v(-1017.92, -72.9) * mm});
            skLineSegment(sketch, "E231.right", {"start": v(-1014.24, -48.18) * mm, "end": v(-1028.46, -62.23) * mm});
            skPoint(sketch, "E231.middle", {"position": v(-1016.08, -60.54) * mm});
            skLineSegment(sketch, "E232.1.0", {"start": v(-876.9, -25.7) * mm, "end": v(-857.6, -30.99) * mm});
            skLineSegment(sketch, "E232.1.1", {"start": v(-872.92, -11.23) * mm, "end": v(-853.63, -16.52) * mm});
            skLineSegment(sketch, "E232.1.2", {"start": v(-853.63, -16.52) * mm, "end": v(-857.6, -30.99) * mm});
            skLineSegment(sketch, "E232.1.3", {"start": v(-872.92, -11.23) * mm, "end": v(-876.9, -25.7) * mm});
            skLineSegment(sketch, "E232.1.4", {"start": v(-949.55, 177.44) * mm, "end": v(-957.17, -103.6) * mm, "construction": true});
            skLineSegment(sketch, "E232.2.0", {"start": v(-965.03, 82) * mm, "end": v(-970.1, 101.36) * mm});
            skLineSegment(sketch, "E232.2.1", {"start": v(-979.55, 78.21) * mm, "end": v(-984.6, 97.56) * mm});
            skLineSegment(sketch, "E232.2.2", {"start": v(-984.6, 97.56) * mm, "end": v(-970.1, 101.36) * mm});
            skLineSegment(sketch, "E232.2.3", {"start": v(-979.55, 78.21) * mm, "end": v(-965.03, 82) * mm});
            skLineSegment(sketch, "E232.2.4", {"start": v(-1104.63, -82.48) * mm, "end": v(-857.42, 51.44) * mm, "construction": true});
            skArc(sketch, "E233", {"start": v(-1006.8, -47.85) * mm, "mid": v(-1006.84, -51.4) * mm, "end": v(-1003.3, -51.42) * mm});
            skArc(sketch, "E234", {"start": v(-982.07, -30.45) * mm, "mid": v(-981.88, -26.86) * mm, "end": v(-985.47, -26.78) * mm});
            skLineSegment(sketch, "E235", {"start": v(-1006.8, -47.85) * mm, "end": v(-985.47, -26.78) * mm});
            skLineSegment(sketch, "E236", {"start": v(-982.07, -30.45) * mm, "end": v(-1003.3, -51.42) * mm});
            skLineSegment(sketch, "E237.1.0", {"start": v(-880.9, -19.4) * mm, "end": v(-909.8, -11.48) * mm});
            skLineSegment(sketch, "E237.1.1", {"start": v(-908.33, -6.7) * mm, "end": v(-879.55, -14.6) * mm});
            skArc(sketch, "E237.1.2", {"start": v(-908.33, -6.7) * mm, "mid": v(-911.53, -8.33) * mm, "end": v(-909.8, -11.48) * mm});
            skArc(sketch, "E237.1.3", {"start": v(-880.9, -19.4) * mm, "mid": v(-877.8, -17.68) * mm, "end": v(-879.55, -14.6) * mm});
            skLineSegment(sketch, "E237.2.0", {"start": v(-968.47, 75.4) * mm, "end": v(-960.9, 46.4) * mm});
            skLineSegment(sketch, "E237.2.1", {"start": v(-965.76, 45.3) * mm, "end": v(-973.32, 74.16) * mm});
            skArc(sketch, "E237.2.2", {"start": v(-965.76, 45.3) * mm, "mid": v(-962.76, 43.33) * mm, "end": v(-960.9, 46.4) * mm});
            skArc(sketch, "E237.2.3", {"start": v(-968.47, 75.4) * mm, "mid": v(-971.52, 77.21) * mm, "end": v(-973.32, 74.16) * mm});
            skLineSegment(sketch, "E238", {"start": v(-1114.66, -66.31) * mm, "end": v(-1078.4, -3.49) * mm, "construction": true});
            skPoint(sketch, "E239", {"position": v(-1078.11, -3) * mm});
            skLineSegment(sketch, "E240", {"start": v(-1041.57, 60.3) * mm, "end": v(-1009.33, 116.16) * mm, "construction": true});
            skPoint(sketch, "E241", {"position": v(-1009.03, 116.69) * mm});
            skLineSegment(sketch, "E242", {"start": v(-1090.65, -107.9) * mm, "end": v(-1023.68, -107.9) * mm, "construction": true});
            skLineSegment(sketch, "E243", {"start": v(-789.82, -65.75) * mm, "end": v(-827.16, -1.25) * mm, "construction": true});
            skPoint(sketch, "E244", {"position": v(-1021.53, -107.9) * mm});
            skPoint(sketch, "E245", {"position": v(-883.27, -107.9) * mm});
            skPoint(sketch, "E246", {"position": v(-806.3, -37.3) * mm});
            skArc(sketch, "E247", {"start": v(-1019.38, -87.9) * mm, "mid": v(-1021.55, -85.74) * mm, "end": v(-1023.68, -87.93) * mm});
            skArc(sketch, "E248", {"start": v(-881.13, -88) * mm, "mid": v(-883.37, -85.74) * mm, "end": v(-885.4, -88.2) * mm});
            skArc(sketch, "E249", {"start": v(-828.97, -37.98) * mm, "mid": v(-829.76, -40.91) * mm, "end": v(-826.82, -41.7) * mm});
            skArc(sketch, "E250", {"start": v(-991.85, 106.07) * mm, "mid": v(-989.07, 107.07) * mm, "end": v(-989.92, 109.9) * mm});
            skArc(sketch, "E251", {"start": v(-1061.13, -13.45) * mm, "mid": v(-1058.19, -12.66) * mm, "end": v(-1058.98, -9.73) * mm});
            skLineSegment(sketch, "E252", {"start": v(-989.92, 109.9) * mm, "end": v(-1007.19, 119.87) * mm});
            skLineSegment(sketch, "E253", {"start": v(-1023.68, -87.85) * mm, "end": v(-1023.68, -107.9) * mm});
            skLineSegment(sketch, "E254", {"start": v(-1019.38, -87.9) * mm, "end": v(-1019.38, -107.9) * mm});
            skLineSegment(sketch, "E255", {"start": v(-885.4, -88.2) * mm, "end": v(-885.4, -107.9) * mm});
            skLineSegment(sketch, "E256", {"start": v(-881.13, -88) * mm, "end": v(-881.13, -107.9) * mm});
            skLineSegment(sketch, "E257.trimOffspring", {"start": v(-881.13, -107.9) * mm, "end": v(-814.15, -107.9) * mm, "construction": true});
            skLineSegment(sketch, "E258.trimOffspring", {"start": v(-883.27, -107.9) * mm, "end": v(-814.15, -107.9) * mm});
            skLineSegment(sketch, "E259", {"start": v(-1076.24, 0.24) * mm, "end": v(-1058.98, -9.73) * mm});
            skLineSegment(sketch, "E260", {"start": v(-1061.13, -13.45) * mm, "end": v(-1078.4, -3.49) * mm});
            skLineSegment(sketch, "E261.trimOffspring", {"start": v(-1076.24, 0.24) * mm, "end": v(-1041.57, 60.3) * mm, "construction": true});
            skLineSegment(sketch, "E262.trimOffspring", {"start": v(-1076.24, 0.24) * mm, "end": v(-1009.33, 116.16) * mm});
            skLineSegment(sketch, "E263", {"start": v(-991.85, 106.07) * mm, "end": v(-1009.33, 116.16) * mm});
            skLineSegment(sketch, "E264.trimOffspring", {"start": v(-1007.19, 119.87) * mm, "end": v(-976.48, 173.08) * mm, "construction": true});
            skLineSegment(sketch, "E265.trimOffspring", {"start": v(-1007.19, 119.87) * mm, "end": v(-976.48, 173.08) * mm});
            skLineSegment(sketch, "E266.trimOffspring", {"start": v(-827.1, -1.22) * mm, "end": v(-928.48, 174.24) * mm, "construction": true});
            skLineSegment(sketch, "E267", {"start": v(-811.7, -27.97) * mm, "end": v(-828.97, -37.98) * mm});
            skLineSegment(sketch, "E268", {"start": v(-826.82, -41.7) * mm, "end": v(-809.57, -31.72) * mm});
            skLineSegment(sketch, "E269.trimOffspring", {"start": v(-811.72, -28) * mm, "end": v(-827.16, -1.25) * mm});
            skLineSegment(sketch, "E270.trimOffspring", {"start": v(-1019.38, -107.9) * mm, "end": v(-952.4, -107.9) * mm, "construction": true});
            skLineSegment(sketch, "E271.trimOffspring", {"start": v(-1019.38, -107.9) * mm, "end": v(-885.4, -107.9) * mm});
            skArc(sketch, "E272", {"start": v(-565.12, -81.34) * mm, "mid": v(-567.27, -79.2) * mm, "end": v(-569.42, -81.34) * mm});
            skArc(sketch, "E273", {"start": v(-342.87, -81.34) * mm, "mid": v(-345.05, -79.2) * mm, "end": v(-347.17, -81.39) * mm});
            skArc(sketch, "E274", {"start": v(-569.42, -96.32) * mm, "mid": v(-567.28, -98.49) * mm, "end": v(-565.12, -96.34) * mm});
            skLineSegment(sketch, "E275", {"start": v(-569.42, -96.32) * mm, "end": v(-569.42, -81.34) * mm});
            skLineSegment(sketch, "E276", {"start": v(-565.12, -81.34) * mm, "end": v(-565.12, -96.34) * mm});
            skArc(sketch, "E277", {"start": v(-347.17, -96.34) * mm, "mid": v(-345.02, -98.49) * mm, "end": v(-342.87, -96.34) * mm});
            skLineSegment(sketch, "E278", {"start": v(-347.17, -81.3) * mm, "end": v(-347.17, -96.34) * mm});
            skLineSegment(sketch, "E279", {"start": v(-342.87, -81.34) * mm, "end": v(-342.87, -96.34) * mm});
            skSolve(sketch);
        }
        {
            var Q0;
            Q0=makeQuery(id+"F2.imprint","IMPRINT",FACE,{"disambiguationData":[TD([[makeQuery(id+"F2.imprint","IMPRINT",EDGE,{"derivedFrom":sQuery(id+"F2.wireOp",EDGE,"E116")}),1.0]])]});
            var Q1;
            {var subQ4=sQuery(id+"F2.wireOp",EDGE,"E120");Q1=makeQuery(id+"F2.imprint","IMPRINT",FACE,{"disambiguationData":[TD([[makeQuery(id+"F2.imprint","IMPRINT",EDGE,{"derivedFrom":subQ4}),-1.0]])]});}
            var Q2;
            {var subQ0=sQuery(id+"F2.wireOp",EDGE,"59f0e6ae-0bd1-4321-8c80-2a786149494e.trimOffspring");Q2=makeQuery(id+"F2.imprint","IMPRINT",FACE,{"disambiguationData":[TD([[makeQuery(id+"F2.imprint","IMPRINT",EDGE,{"derivedFrom":subQ0}),1.0]])]});}
            var Q3;
            {var subQ4=sQuery(id+"F2.wireOp",EDGE,"59f0e6ae-0bd1-4321-8c80-2a786149494e.trimOffspring");Q3=makeQuery(id+"F2.imprint","IMPRINT",FACE,{"disambiguationData":[TD([[makeQuery(id+"F2.imprint","IMPRINT",EDGE,{"derivedFrom":subQ4}),-1.0]])]});}
            var Q4;
            {var subQ6=sQuery(id+"F2.wireOp",EDGE,"E120");var subQ7=sQuery(id+"F2.wireOp",EDGE,"E118.2.0");var subQ8=makeQuery(id+"F2.imprint","INTERSECT",VERTEX,{"derivedFrom":[subQ7,subQ6]});Q4=makeQuery(id+"F2.imprint","IMPRINT",FACE,{"disambiguationData":[TD([[makeQuery(id+"F2.imprint","IMPRINT",EDGE,{"disambiguationData":[TD([[subQ8,-1.0]])],"derivedFrom":subQ7}),1.0]])]});}
            var Q5;
            {var subQ0=sQuery(id+"F2.wireOp",EDGE,"E135");Q5=makeQuery(id+"F2.imprint","IMPRINT",FACE,{"disambiguationData":[TD([[makeQuery(id+"F2.imprint","IMPRINT",EDGE,{"derivedFrom":subQ0}),-1.0]])]});}
            var Q6;
            {var subQ1=sQuery(id+"F2.wireOp",EDGE,"E121");var subQ3=sQuery(id+"F2.wireOp",EDGE,"E133");var subQ4=makeQuery(id+"F2.imprint","INTERSECT",VERTEX,{"derivedFrom":[subQ1,subQ3]});Q6=makeQuery(id+"F2.imprint","IMPRINT",FACE,{"disambiguationData":[TD([[makeQuery(id+"F2.imprint","IMPRINT",EDGE,{"disambiguationData":[TD([[subQ4,-1.0]])],"derivedFrom":subQ3}),-1.0]])]});}
            extrude(context, id + "F3", {"entities" : qUnion([Q0, Q1, Q2, Q3, Q4, Q5, Q6]), "oppositeDirection" : true, "depth" : 5 * mm, "offsetDistance" : 25 * mm});
        }
        {
            var Q0;
            Q0=makeQuery(id+"F2.imprint","IMPRINT",FACE,{"disambiguationData":[TD([[makeQuery(id+"F2.imprint","IMPRINT",EDGE,{"derivedFrom":sQuery(id+"F2.wireOp",EDGE,"E118.1.0")}),1.0]])]});
            var Q1;
            {var subQ0=sQuery(id+"F2.wireOp",EDGE,"E132");var subQ1=sQuery(id+"F2.wireOp",EDGE,"E118.2.0");var subQ3=makeQuery(id+"F2.imprint","INTERSECT",VERTEX,{"derivedFrom":[subQ1,subQ0]});Q1=makeQuery(id+"F2.imprint","IMPRINT",FACE,{"disambiguationData":[TD([[makeQuery(id+"F2.imprint","IMPRINT",EDGE,{"disambiguationData":[TD([[subQ3,-1.0]])],"derivedFrom":subQ1}),1.0]])]});}
            extrude(context, id + "F4", {"entities" : qUnion([Q0, Q1]), "oppositeDirection" : true, "depth" : 50 * mm, "offsetDistance" : 25 * mm});
        }
    });
